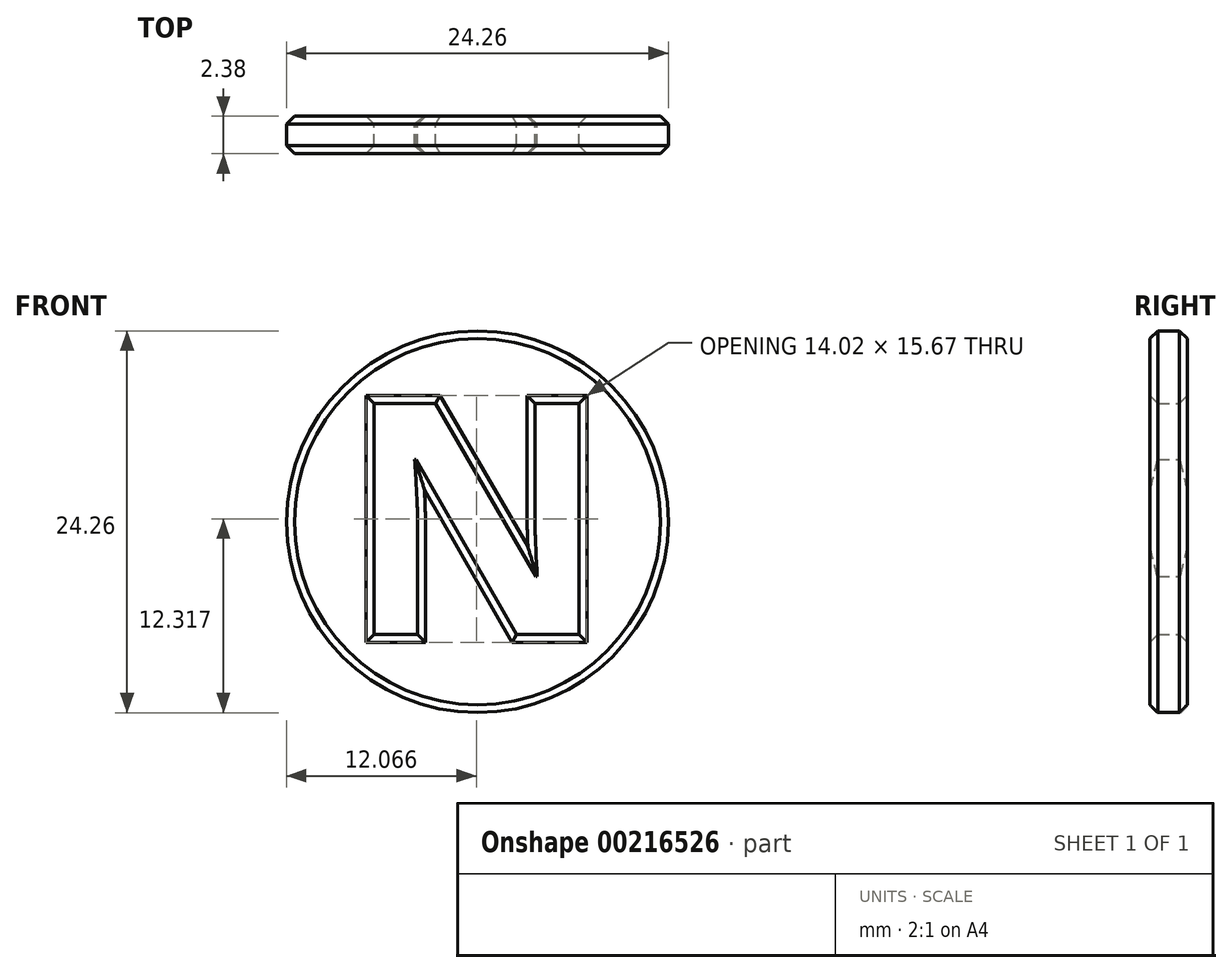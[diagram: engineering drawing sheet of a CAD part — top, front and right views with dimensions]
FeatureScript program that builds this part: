
annotation { "Feature Type Name" : "Feature", "Feature Type Description" : "" }
export const myFeature = defineFeature(function(context is Context, id is Id, definition is map)
    precondition{}
    {
        {
            var Q0;
            Q0=qCreatedBy(makeId("Front.planeOp"),FACE);
            var sketch = newSketch(context, id + "F0", { "sketchPlane" : qUnion([Q0])});
            skCircle(sketch, "E0", {"center": v(0, 0) * mm, "radius": 12.13 * mm});
            skText(sketch, "E1", { "text": "N", "fontName": "OpenSans-Bold.ttf"});
            const initialGuessF0  = {"E1": [-0.00842, -0.00715, 1, 0, 0.0148]};
            skSetInitialGuess(sketch, initialGuessF0);
            skSolve(sketch);
        }
        {
            var Q0;
            Q0=makeQuery(id+"F0.imprint","IMPRINT",FACE,{"disambiguationData":[TD([[makeQuery(id+"F0.imprint","IMPRINT",EDGE,{"derivedFrom":sQuery(id+"F0.wireOp",EDGE,"E0")}),1.0]])]});
            extrude(context, id + "F1", {"entities" : qUnion([Q0]), "depth" : 2.38 * mm});
        }
        {
            var Q0;
            Q0=makeQuery(id+"F1.opExtrude","CAP_FACE",FACE,{"disambiguationData":[OSD([sQuery(id+"F0.wireOp",EDGE,"E0"),sQuery(id+"F0.wireOp",EDGE,"E1.sketch_text.stroke-0"),sQuery(id+"F0.wireOp",EDGE,"E1.sketch_text.stroke-1"),sQuery(id+"F0.wireOp",EDGE,"E1.sketch_text.stroke-2"),sQuery(id+"F0.wireOp",EDGE,"E1.sketch_text.stroke-3"),sQuery(id+"F0.wireOp",EDGE,"E1.sketch_text.stroke-4"),sQuery(id+"F0.wireOp",EDGE,"E1.sketch_text.stroke-5"),sQuery(id+"F0.wireOp",EDGE,"E1.sketch_text.stroke-6"),sQuery(id+"F0.wireOp",EDGE,"E1.sketch_text.stroke-7"),sQuery(id+"F0.wireOp",EDGE,"E1.sketch_text.stroke-8"),sQuery(id+"F0.wireOp",EDGE,"E1.sketch_text.stroke-9"),sQuery(id+"F0.wireOp",EDGE,"E1.sketch_text.stroke-10"),sQuery(id+"F0.wireOp",EDGE,"E1.sketch_text.stroke-11"),sQuery(id+"F0.wireOp",EDGE,"E1.sketch_text.stroke-12"),sQuery(id+"F0.wireOp",EDGE,"E1.sketch_text.stroke-13")])],"isStart":false});
            var Q1;
            Q1=makeQuery(id+"F1.opExtrude","CAP_FACE",FACE,{"disambiguationData":[OSD([sQuery(id+"F0.wireOp",EDGE,"E0"),sQuery(id+"F0.wireOp",EDGE,"E1.sketch_text.stroke-0"),sQuery(id+"F0.wireOp",EDGE,"E1.sketch_text.stroke-1"),sQuery(id+"F0.wireOp",EDGE,"E1.sketch_text.stroke-2"),sQuery(id+"F0.wireOp",EDGE,"E1.sketch_text.stroke-3"),sQuery(id+"F0.wireOp",EDGE,"E1.sketch_text.stroke-4"),sQuery(id+"F0.wireOp",EDGE,"E1.sketch_text.stroke-5"),sQuery(id+"F0.wireOp",EDGE,"E1.sketch_text.stroke-6"),sQuery(id+"F0.wireOp",EDGE,"E1.sketch_text.stroke-7"),sQuery(id+"F0.wireOp",EDGE,"E1.sketch_text.stroke-8"),sQuery(id+"F0.wireOp",EDGE,"E1.sketch_text.stroke-9"),sQuery(id+"F0.wireOp",EDGE,"E1.sketch_text.stroke-10"),sQuery(id+"F0.wireOp",EDGE,"E1.sketch_text.stroke-11"),sQuery(id+"F0.wireOp",EDGE,"E1.sketch_text.stroke-12"),sQuery(id+"F0.wireOp",EDGE,"E1.sketch_text.stroke-13")])],"isStart":true});
            chamfer(context, id + "F2", {"entities" : qUnion([Q0, Q1]), "width" : .5 * mm, "tangentPropagation" : true});
        }
    });
